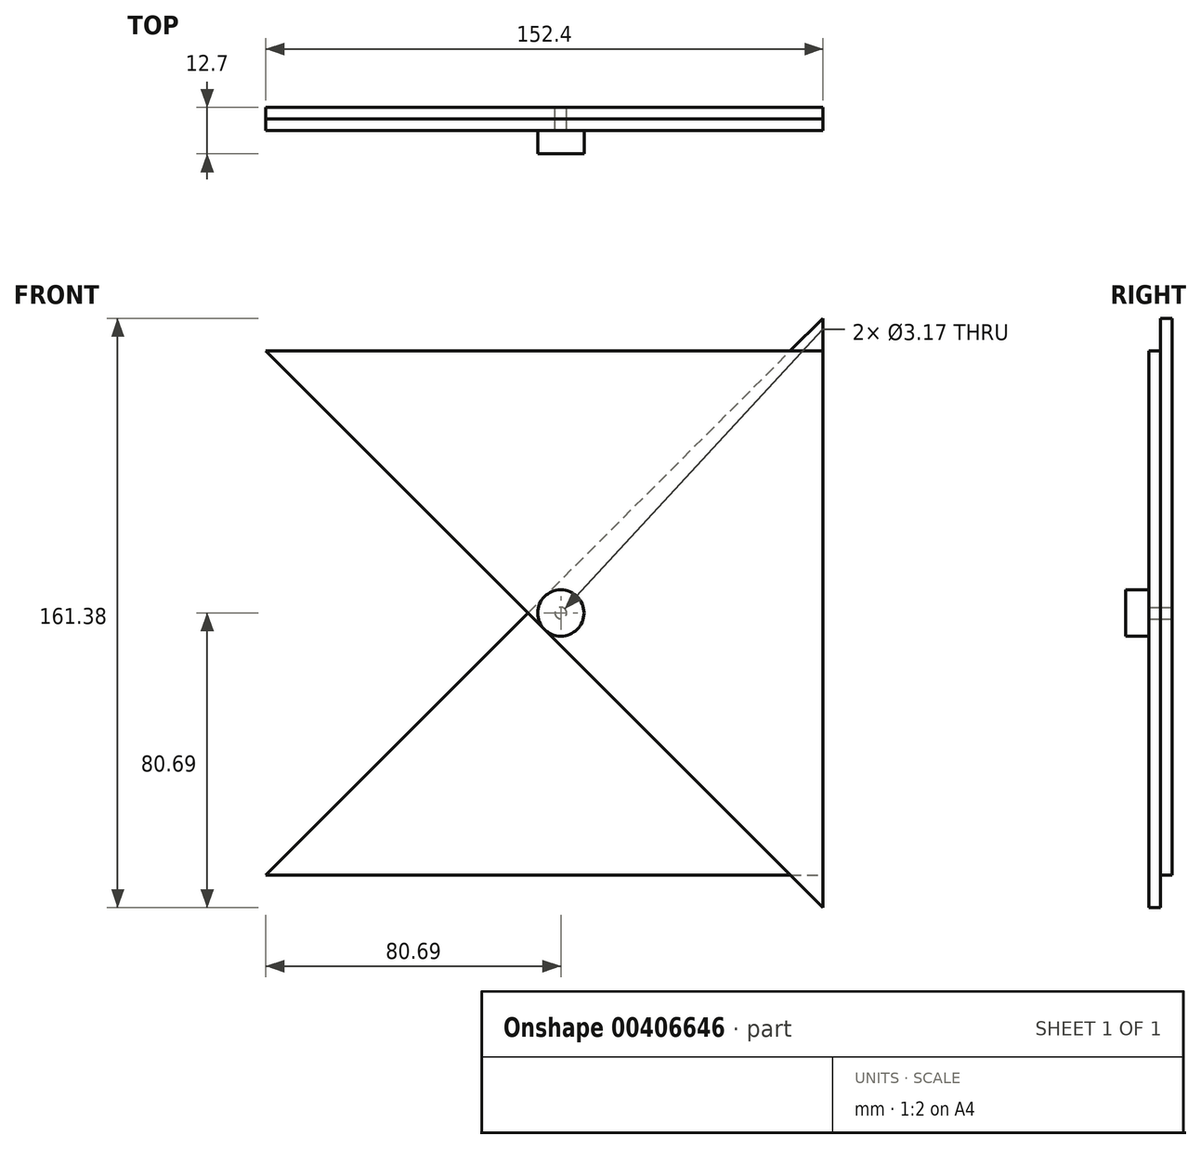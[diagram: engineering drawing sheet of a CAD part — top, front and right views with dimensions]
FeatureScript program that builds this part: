
annotation { "Feature Type Name" : "Feature", "Feature Type Description" : "" }
export const myFeature = defineFeature(function(context is Context, id is Id, definition is map)
    precondition{}
    {
        {
            var Q0;
            Q0=qCreatedBy(makeId("Front.planeOp"),FACE);
            var sketch = newSketch(context, id + "F0", { "sketchPlane" : qUnion([Q0])});
            skLineSegment(sketch, "E0.bottom", {"start": v(-76.2, 76.2) * mm, "end": v(76.2, 76.2) * mm, "construction": true});
            skLineSegment(sketch, "E0.top", {"start": v(-76.2, -76.2) * mm, "end": v(76.2, -76.2) * mm});
            skLineSegment(sketch, "E0.left", {"start": v(-76.2, 76.2) * mm, "end": v(-76.2, -76.2) * mm, "construction": true});
            skLineSegment(sketch, "E0.right", {"start": v(76.2, 76.2) * mm, "end": v(76.2, -76.2) * mm});
            skPoint(sketch, "E0.middle", {"position": v(0, 0) * mm});
            skLineSegment(sketch, "E1", {"start": v(-76.2, -76.2) * mm, "end": v(76.2, 76.2) * mm});
            skLineSegment(sketch, "E2", {"start": v(-76.2, 76.2) * mm, "end": v(76.2, -76.2) * mm, "construction": true});
            skCircle(sketch, "E3", {"center": v(4.5, -4.5) * mm, "radius": 6.35 * mm, "construction": true});
            skCircle(sketch, "E4", {"center": v(4.5, -4.5) * mm, "radius": 1.59 * mm});
            skSolve(sketch);
        }
        {
            var Q0;
            Q0 = qSketchRegion(id + "F0", true);
            var Q1;
            Q1=sQuery(id+"F0.wireOp",EDGE,"E0.bottom");
            var Q2;
            Q2=sQuery(id+"F0.wireOp",EDGE,"E0.left");
            extrude(context, id + "F1", {"entities" : qUnion([Q0]), "surfaceEntities" : qUnion([Q1, Q2]), "depth" : 3.17 * mm});
        }
        {
            var Q0;
            Q0=sQuery(id+"F0.wireOp",VERTEX,"E4.center");
            var Q1;
            Q1=qCreatedBy(makeId("Top.planeOp"),FACE);
            cPlane(context, id + "F2", {"entities" : qUnion([Q0, Q1]), "cplaneType" : CPlaneType.PLANE_POINT, "offset" : 25.4 * mm, "width" : 152.4 * mm, "height" : 152.4 * mm});
        }
        {
            var Q0;
            Q0=qCreatedBy(id+"F2.planeOp",FACE);
            var sketch = newSketch(context, id + "F3", { "sketchPlane" : qUnion([Q0])});
            skPoint(sketch, "E5.0", {"position": v(4.5, 0) * mm});
            skLineSegment(sketch, "E6", {"start": v(4.5, 0) * mm, "end": v(4.5, -119.12) * mm});
            skSolve(sketch);
        }
        {
            var Q0;
            Q0=makeQuery(id+"F1.opExtrude","SWEPT_BODY",BODY,{"disambiguationData":[OSD([sQuery(id+"F0.wireOp",EDGE,"E0.top"),sQuery(id+"F0.wireOp",EDGE,"E0.right"),sQuery(id+"F0.wireOp",EDGE,"E1"),sQuery(id+"F0.wireOp",EDGE,"E4")])]});
            var Q1;
            Q1=sQuery(id+"F3.wireOp",EDGE,"E6");
            var Q2;
            Q2=sQuery(id+"F3.wireOp",EDGE,"E6");
            transform(context, id + "F4", {"entities" : qUnion([Q0]), "transformType" : TransformType.ROTATION, "transformAxis" : qUnion([Q2]), "angle" : 90 * degree, "makeCopy" : true});
        }
        {
            var Q0;
            Q0=makeQuery(id+"F4.opPattern","COPY",BODY,{"derivedFrom":makeQuery(id+"F1.opExtrude","SWEPT_BODY",BODY,{"disambiguationData":[OSD([sQuery(id+"F0.wireOp",EDGE,"E0.top"),sQuery(id+"F0.wireOp",EDGE,"E0.right"),sQuery(id+"F0.wireOp",EDGE,"E1"),sQuery(id+"F0.wireOp",EDGE,"E4")])]}),"instanceName":"1"});
            var Q1;
            Q1=sQuery(id+"F3.wireOp",EDGE,"E6");
            transform(context, id + "F5", {"entities" : qUnion([Q0]), "transformType" : TransformType.TRANSLATION_DISTANCE, "transformDirection" : qUnion([Q1]), "distance" : 3.17 * mm, "makeCopy" : false});
        }
        {
            var Q0;
            Q0=makeQuery(id+"F4.opPattern","COPY",FACE,{"derivedFrom":makeQuery(id+"F1.opExtrude","CAP_FACE",FACE,{"disambiguationData":[OSD([sQuery(id+"F0.wireOp",EDGE,"E0.top"),sQuery(id+"F0.wireOp",EDGE,"E0.right"),sQuery(id+"F0.wireOp",EDGE,"E1"),sQuery(id+"F0.wireOp",EDGE,"E4")])],"isStart":false}),"instanceName":"1"});
            var sketch = newSketch(context, id + "F6", { "sketchPlane" : qUnion([Q0])});
            skCircle(sketch, "E7.1", {"center": v(4.5, -4.5) * mm, "radius": 6.35 * mm});
            skSolve(sketch);
        }
        {
            var Q0;
            Q0 = qSketchRegion(id + "F6", true);
            extrude(context, id + "F7", {"entities" : qUnion([Q0]), "depth" : 6.35 * mm});
        }
    });
